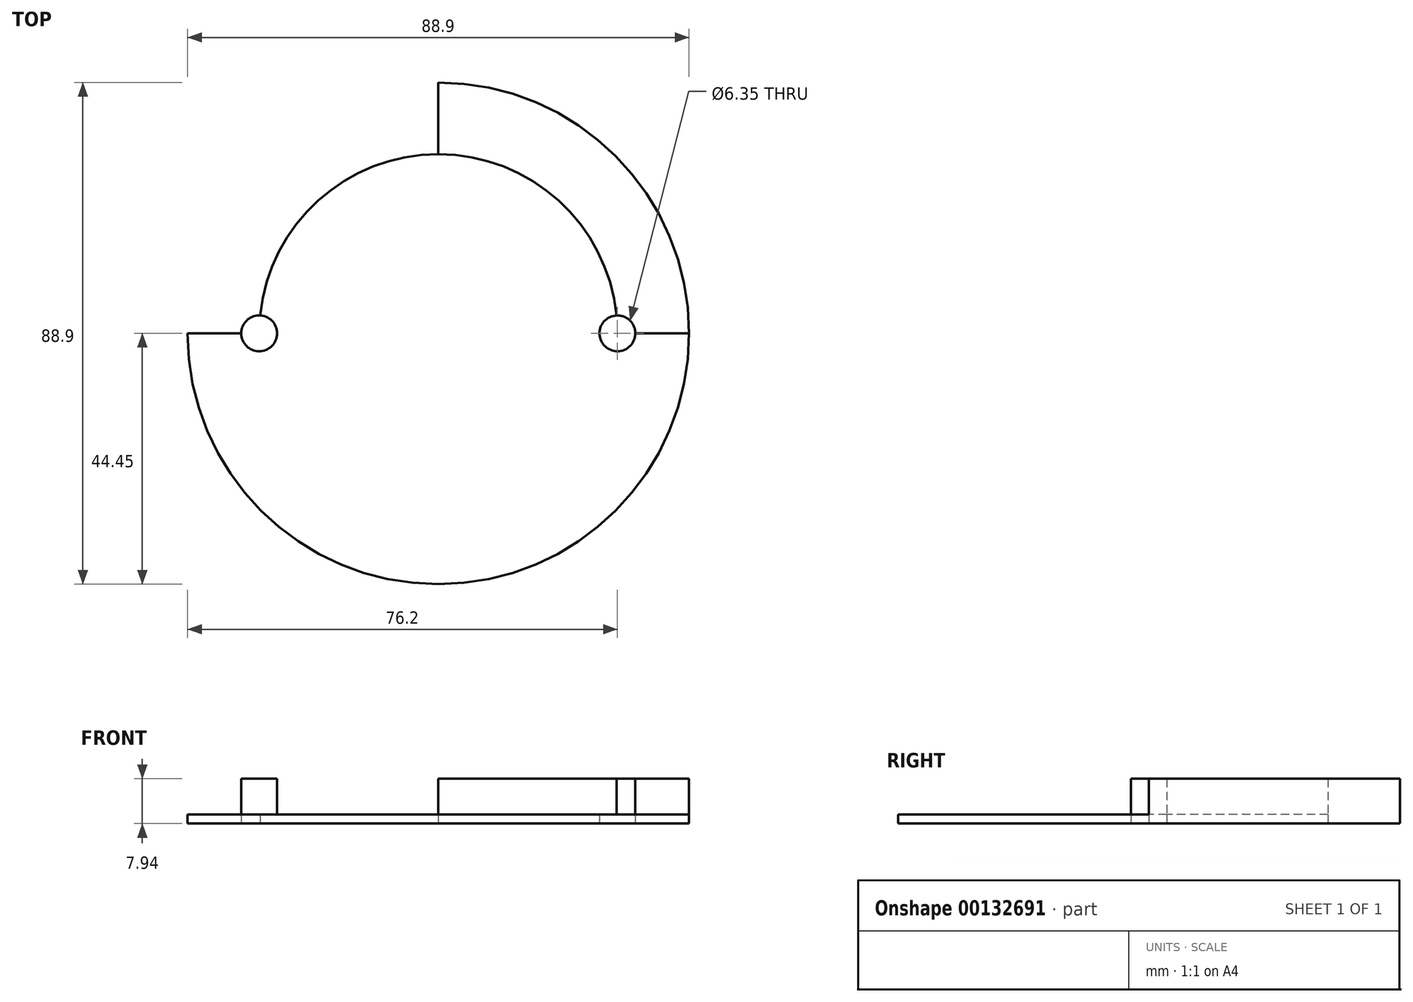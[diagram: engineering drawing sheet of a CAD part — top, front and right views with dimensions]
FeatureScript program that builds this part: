
annotation { "Feature Type Name" : "Feature", "Feature Type Description" : "" }
export const myFeature = defineFeature(function(context is Context, id is Id, definition is map)
    precondition{}
    {
        {
            var Q0;
            Q0=qCreatedBy(makeId("Top.planeOp"),FACE);
            var sketch = newSketch(context, id + "F0", { "sketchPlane" : qUnion([Q0])});
            skCircle(sketch, "E0", {"center": v(0, 0) * mm, "radius": 44.45 * mm});
            skLineSegment(sketch, "E1", {"start": v(0, 72.8) * mm, "end": v(0, -70.66) * mm});
            skArc(sketch, "E2", {"start": v(-31.6, -3.17) * mm, "mid": v(0, -31.75) * mm, "end": v(31.6, -3.17) * mm});
            skLineSegment(sketch, "E3", {"start": v(70.46, 0) * mm, "end": v(34.93, 0) * mm});
            skCircle(sketch, "E4", {"center": v(-31.75, 0) * mm, "radius": 3.18 * mm});
            skCircle(sketch, "E5.MirrorC", {"center": v(31.75, 0) * mm, "radius": 3.18 * mm});
            skLineSegment(sketch, "E6.trimOffspring", {"start": v(-34.92, 0) * mm, "end": v(-64.18, 0) * mm});
            skArc(sketch, "E7.trimOffspring", {"start": v(31.6, 3.17) * mm, "mid": v(0, 31.75) * mm, "end": v(-31.6, 3.17) * mm});
            skLineSegment(sketch, "E8.trimOffspring", {"start": v(28.58, 0) * mm, "end": v(-28.57, 0) * mm});
            skSolve(sketch);
        }
        {
            var Q0;
            {var subQ3=sQuery(id+"F0.wireOp",EDGE,"E6.trimOffspring");var subQ7=sQuery(id+"F0.wireOp",EDGE,"E0");var subQ9=makeQuery(id+"F0.imprint","INTERSECT",VERTEX,{"derivedFrom":[subQ7,subQ3]});Q0=makeQuery(id+"F0.imprint","IMPRINT",FACE,{"disambiguationData":[TD([[makeQuery(id+"F0.imprint","IMPRINT",EDGE,{"disambiguationData":[TD([[subQ9,-1.0]])],"derivedFrom":subQ7}),1.0]])]});}
            var Q1;
            {var subQ0=sQuery(id+"F0.wireOp",EDGE,"E8.trimOffspring");var subQ1=sQuery(id+"F0.wireOp",EDGE,"E1");var subQ2=makeQuery(id+"F0.imprint","INTERSECT",VERTEX,{"derivedFrom":[subQ1,subQ0]});Q1=makeQuery(id+"F0.imprint","IMPRINT",FACE,{"disambiguationData":[TD([[makeQuery(id+"F0.imprint","IMPRINT",EDGE,{"disambiguationData":[TD([[subQ2,-1.0]])],"derivedFrom":subQ1}),-1.0]])]});}
            var Q2;
            {var subQ0=sQuery(id+"F0.wireOp",EDGE,"E8.trimOffspring");var subQ1=sQuery(id+"F0.wireOp",EDGE,"E1");var subQ2=makeQuery(id+"F0.imprint","INTERSECT",VERTEX,{"derivedFrom":[subQ1,subQ0]});Q2=makeQuery(id+"F0.imprint","IMPRINT",FACE,{"disambiguationData":[TD([[makeQuery(id+"F0.imprint","IMPRINT",EDGE,{"disambiguationData":[TD([[subQ2,-1.0]])],"derivedFrom":subQ1}),1.0]])]});}
            var Q3;
            {var subQ1=sQuery(id+"F0.wireOp",EDGE,"E3");var subQ3=sQuery(id+"F0.wireOp",EDGE,"E0");var subQ4=makeQuery(id+"F0.imprint","INTERSECT",VERTEX,{"derivedFrom":[subQ3,subQ1]});Q3=makeQuery(id+"F0.imprint","IMPRINT",FACE,{"disambiguationData":[TD([[makeQuery(id+"F0.imprint","IMPRINT",EDGE,{"disambiguationData":[TD([[subQ4,1.0]])],"derivedFrom":subQ3}),1.0]])]});}
            var Q4;
            {var subQ3=sQuery(id+"F0.wireOp",EDGE,"E0");var subQ5=sQuery(id+"F0.wireOp",EDGE,"E1");var subQ6=makeQuery(id+"F0.imprint","INTERSECT",VERTEX,{"disambiguationData":[OD(0.0)],"derivedFrom":[subQ3,subQ5]});Q4=makeQuery(id+"F0.imprint","IMPRINT",FACE,{"disambiguationData":[TD([[makeQuery(id+"F0.imprint","IMPRINT",EDGE,{"disambiguationData":[TD([[subQ6,1.0]])],"derivedFrom":subQ3}),1.0]])]});}
            var Q5;
            {var subQ0=sQuery(id+"F0.wireOp",EDGE,"E7.trimOffspring");var subQ1=sQuery(id+"F0.wireOp",EDGE,"E1");var subQ2=makeQuery(id+"F0.imprint","INTERSECT",VERTEX,{"derivedFrom":[subQ1,subQ0]});Q5=makeQuery(id+"F0.imprint","IMPRINT",FACE,{"disambiguationData":[TD([[makeQuery(id+"F0.imprint","IMPRINT",EDGE,{"disambiguationData":[TD([[subQ2,-1.0]])],"derivedFrom":subQ1}),1.0]])]});}
            var Q6;
            {var subQ0=sQuery(id+"F0.wireOp",EDGE,"E7.trimOffspring");var subQ1=sQuery(id+"F0.wireOp",EDGE,"E1");var subQ2=makeQuery(id+"F0.imprint","INTERSECT",VERTEX,{"derivedFrom":[subQ1,subQ0]});Q6=makeQuery(id+"F0.imprint","IMPRINT",FACE,{"disambiguationData":[TD([[makeQuery(id+"F0.imprint","IMPRINT",EDGE,{"disambiguationData":[TD([[subQ2,-1.0]])],"derivedFrom":subQ1}),-1.0]])]});}
            var Q7;
            {var subQ5=sQuery(id+"F0.wireOp",EDGE,"E0");var subQ7=sQuery(id+"F0.wireOp",EDGE,"E1");var subQ8=makeQuery(id+"F0.imprint","INTERSECT",VERTEX,{"disambiguationData":[OD(0.0)],"derivedFrom":[subQ5,subQ7]});Q7=makeQuery(id+"F0.imprint","IMPRINT",FACE,{"disambiguationData":[TD([[makeQuery(id+"F0.imprint","IMPRINT",EDGE,{"disambiguationData":[TD([[subQ8,-1.0]])],"derivedFrom":subQ5}),1.0]])]});}
            extrude(context, id + "F1", {"entities" : qUnion([Q0, Q1, Q2, Q3, Q4, Q5, Q6, Q7]), "depth" : 1.59 * mm});
        }
        {
            var Q0;
            {var subQ0=sQuery(id+"F0.wireOp",EDGE,"E4");var subQ1=makeQuery(id+"F0.imprint","INTERSECT",VERTEX,{"derivedFrom":[subQ0,sQuery(id+"F0.wireOp",EDGE,"E7.trimOffspring")]});Q0=makeQuery(id+"F0.imprint","IMPRINT",FACE,{"disambiguationData":[TD([[makeQuery(id+"F0.imprint","IMPRINT",EDGE,{"disambiguationData":[TD([[subQ1,1.0]])],"derivedFrom":subQ0}),1.0]])]});}
            var Q1;
            {var subQ0=sQuery(id+"F0.wireOp",EDGE,"E5.MirrorC");var subQ1=makeQuery(id+"F0.imprint","INTERSECT",VERTEX,{"derivedFrom":[subQ0,sQuery(id+"F0.wireOp",EDGE,"E7.trimOffspring")]});Q1=makeQuery(id+"F0.imprint","IMPRINT",FACE,{"disambiguationData":[TD([[makeQuery(id+"F0.imprint","IMPRINT",EDGE,{"disambiguationData":[TD([[subQ1,1.0]])],"derivedFrom":subQ0}),-1.0]])]});}
            extrude(context, id + "F2", {"entities" : qUnion([Q0, Q1]), "operationType" : NewBodyOperationType.ADD, "depth" : 7.94 * mm});
        }
    });
